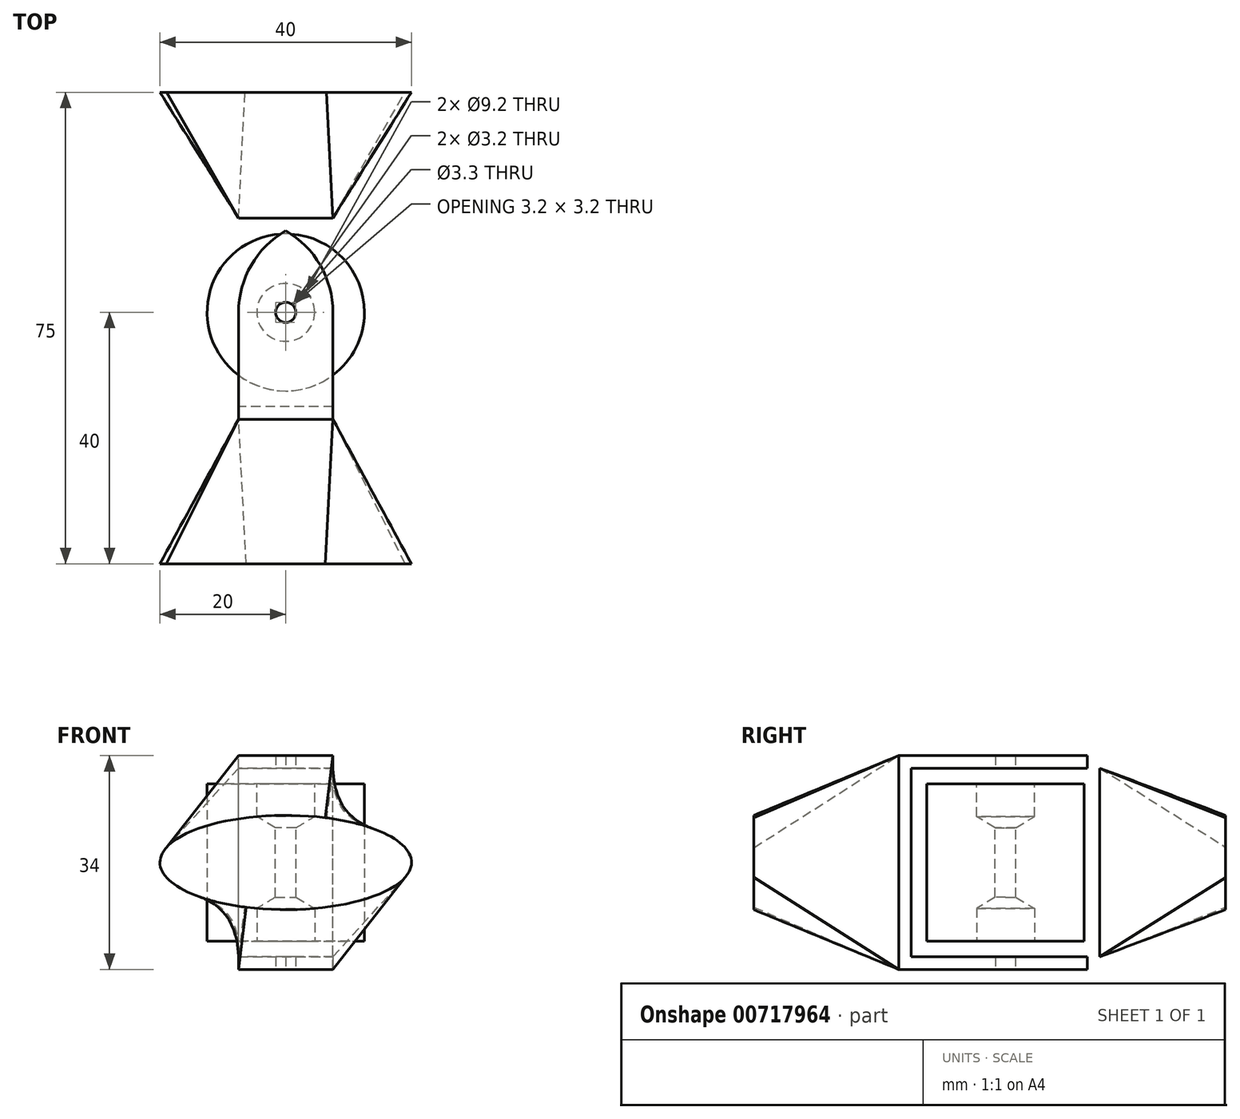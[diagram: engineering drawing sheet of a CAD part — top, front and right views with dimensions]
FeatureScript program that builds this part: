
annotation { "Feature Type Name" : "Feature", "Feature Type Description" : "" }
export const myFeature = defineFeature(function(context is Context, id is Id, definition is map)
    precondition{}
    {
        {
            var Q0;
            Q0=qCreatedBy(makeId("Front.planeOp"),FACE);
            var sketch = newSketch(context, id + "F0", { "sketchPlane" : qUnion([Q0])});
            skLineSegment(sketch, "E0.bottom", {"start": v(7.5, -15) * mm, "end": v(-7.5, -15) * mm});
            skLineSegment(sketch, "E0.top", {"start": v(7.5, 15) * mm, "end": v(-7.5, 15) * mm});
            skLineSegment(sketch, "E0.left", {"start": v(7.5, -15) * mm, "end": v(7.5, 15) * mm});
            skLineSegment(sketch, "E0.right", {"start": v(-7.5, -15) * mm, "end": v(-7.5, 15) * mm});
            skPoint(sketch, "E0.middle", {"position": v(0, 0) * mm});
            skSolve(sketch);
        }
        {
            var Q0;
            Q0 = qSketchRegion(id + "F0", true);
            extrude(context, id + "F1", {"entities" : qUnion([Q0]), "depth" : 2 * mm, "offsetDistance" : 25 * mm});
        }
        {
            var Q0;
            Q0=qCreatedBy(makeId("Top.planeOp"),FACE);
            var sketch = newSketch(context, id + "F2", { "sketchPlane" : qUnion([Q0])});
            skCircle(sketch, "E1", {"center": v(0, 15) * mm, "radius": 12.5 * mm});
            skSolve(sketch);
        }
        {
            var Q0;
            Q0 = qSketchRegion(id + "F2", true);
            extrude(context, id + "F3", {"entities" : qUnion([Q0]), "endBound" : BoundingType.SYMMETRIC, "depth" : 25 * mm, "offsetDistance" : 25 * mm});
        }
        {
            var Q0;
            Q0=makeQuery(id+"F1.opExtrude","CAP_FACE",FACE,{"disambiguationData":[OSD([sQuery(id+"F0.wireOp",EDGE,"E0.bottom"),sQuery(id+"F0.wireOp",EDGE,"E0.top"),sQuery(id+"F0.wireOp",EDGE,"E0.left"),sQuery(id+"F0.wireOp",EDGE,"E0.right")])],"isStart":false});
            var sketch = newSketch(context, id + "F4", { "sketchPlane" : qUnion([Q0])});
            skLineSegment(sketch, "E2.bottom", {"start": v(-7.5, -15) * mm, "end": v(7.5, -15) * mm});
            skLineSegment(sketch, "E2.top", {"start": v(-7.5, -17) * mm, "end": v(7.5, -17) * mm});
            skLineSegment(sketch, "E2.left", {"start": v(7.5, -15) * mm, "end": v(7.5, -17) * mm});
            skLineSegment(sketch, "E2.right", {"start": v(-7.5, -15) * mm, "end": v(-7.5, -17) * mm});
            skLineSegment(sketch, "E3.bottom", {"start": v(-7.5, 15) * mm, "end": v(7.5, 15) * mm});
            skLineSegment(sketch, "E3.top", {"start": v(-7.5, 17) * mm, "end": v(7.5, 17) * mm});
            skLineSegment(sketch, "E3.left", {"start": v(7.5, 15) * mm, "end": v(7.5, 17) * mm});
            skLineSegment(sketch, "E3.right", {"start": v(-7.5, 15) * mm, "end": v(-7.5, 17) * mm});
            skSolve(sketch);
        }
        {
            var Q0;
            Q0 = qSketchRegion(id + "F4", true);
            extrude(context, id + "F5", {"entities" : qUnion([Q0]), "operationType" : NewBodyOperationType.ADD, "oppositeDirection" : true, "depth" : 32 * mm, "offsetDistance" : 25 * mm});
        }
        {
            var Q0;
            Q0=makeQuery(id+"F5.opExtrude","CAP_EDGE",EDGE,{"disambiguationData":[OSD([sQuery(id+"F4.wireOp",EDGE,"E3.right")])],"isStart":false});
            var Q1;
            Q1=makeQuery(id+"F5.opExtrude","CAP_EDGE",EDGE,{"disambiguationData":[OSD([sQuery(id+"F4.wireOp",EDGE,"E3.left")])],"isStart":false});
            var Q2;
            Q2=makeQuery(id+"F5.opExtrude","CAP_EDGE",EDGE,{"disambiguationData":[OSD([sQuery(id+"F4.wireOp",EDGE,"E2.left")])],"isStart":false});
            var Q3;
            Q3=makeQuery(id+"F5.opExtrude","CAP_EDGE",EDGE,{"disambiguationData":[OSD([sQuery(id+"F4.wireOp",EDGE,"E2.right")])],"isStart":false});
            fillet(context, id + "F6", {"entities" : qUnion([Q0, Q1, Q2, Q3]), "radius" : 15 * mm, "tangentPropagation" : true, "allowEdgeOverflow" : false});
        }
        {
            var Q0;
            Q0=makeQuery(id+"F3.opExtrude","CAP_FACE",FACE,{"disambiguationData":[OSD([sQuery(id+"F2.wireOp",EDGE,"E1")])],"isStart":false});
            var sketch = newSketch(context, id + "F7", { "sketchPlane" : qUnion([Q0])});
            skPoint(sketch, "E4", {"position": v(0, 15) * mm});
            skSolve(sketch);
        }
        {
            var Q0;
            Q0=sQuery(id+"F7.wireOp",VERTEX,"E4");
            var Q1;
            Q1=makeQuery(id+"F3.opExtrude","SWEPT_BODY",BODY,{"disambiguationData":[OSD([sQuery(id+"F2.wireOp",EDGE,"E1")])]});
            hole(context, id + "F8", {"style" : HoleStyle.SIMPLE, "endStyle" : HoleEndStyle.THROUGH, "standardTappedOrClearance" : lookupTablePath({ "fit" : "Normal", "standard" : "ISO", "size" : "M3", "type" : "Clearance" }), "standardBlindInLast" : lookupTablePath({ "fit" : "Standard", "standard" : "ISO", "size" : "M3", "type" : "Clearance" }), "holeDiameter" : 3.3 * mm, "majorDiameter" : 5 * mm, "isTappedThrough" : true, "tappedDepth" : 12 * mm, "tapClearance" : 3, "locations" : qUnion([Q0]), "scope" : qUnion([Q1])});
        }
        {
            var Q0;
            Q0=makeQuery(id+"F3.opExtrude","CAP_FACE",FACE,{"disambiguationData":[OSD([sQuery(id+"F2.wireOp",EDGE,"E1")])],"isStart":false});
            var sketch = newSketch(context, id + "F9", { "sketchPlane" : qUnion([Q0])});
            skPoint(sketch, "E5", {"position": v(0, 15) * mm});
            skSolve(sketch);
        }
        {
            var Q0;
            Q0=sQuery(id+"F9.wireOp",VERTEX,"E5");
            var Q1;
            Q1=makeQuery(id+"F3.opExtrude","SWEPT_BODY",BODY,{"disambiguationData":[OSD([sQuery(id+"F2.wireOp",EDGE,"E1")])]});
            hole(context, id + "F10", {"style" : HoleStyle.SIMPLE, "endStyle" : HoleEndStyle.BLIND, "standardTappedOrClearance" : lookupTablePath({ "fit" : "Normal", "standard" : "Custom", "size" : "M5", "type" : "Clearance" }), "standardBlindInLast" : lookupTablePath({ "fit" : "Standard", "standard" : "Custom", "size" : "M5", "type" : "Clearance" }), "holeDiameter" : 9.2 * mm, "majorDiameter" : 5 * mm, "holeDepth" : 5.2 * mm, "isTappedThrough" : true, "tappedDepth" : 12 * mm, "tapClearance" : 3, "locations" : qUnion([Q0]), "scope" : qUnion([Q1])});
        }
        {
            var Q0;
            Q0=makeQuery(id+"F3.opExtrude","CAP_FACE",FACE,{"disambiguationData":[OSD([sQuery(id+"F2.wireOp",EDGE,"E1")])],"isStart":true});
            var sketch = newSketch(context, id + "F11", { "sketchPlane" : qUnion([Q0])});
            skPoint(sketch, "E6", {"position": v(0, -15) * mm});
            skSolve(sketch);
        }
        {
            var Q0;
            Q0=sQuery(id+"F11.wireOp",VERTEX,"E6");
            var Q1;
            Q1=makeQuery(id+"F3.opExtrude","SWEPT_BODY",BODY,{"disambiguationData":[OSD([sQuery(id+"F2.wireOp",EDGE,"E1")])]});
            hole(context, id + "F12", {"style" : HoleStyle.SIMPLE, "endStyle" : HoleEndStyle.BLIND, "holeDiameter" : 9.2 * mm, "majorDiameter" : 5 * mm, "holeDepth" : 5.2 * mm, "isTappedThrough" : true, "tappedDepth" : 12 * mm, "tapClearance" : 3, "locations" : qUnion([Q0]), "scope" : qUnion([Q1])});
        }
        {
            var Q0;
            Q0=makeQuery(id+"F5.opExtrude","SWEPT_FACE",FACE,{"disambiguationData":[OSD([sQuery(id+"F4.wireOp",EDGE,"E2.top")])]});
            var sketch = newSketch(context, id + "F13", { "sketchPlane" : qUnion([Q0])});
            skPoint(sketch, "E7", {"position": v(0, -15) * mm});
            skSolve(sketch);
        }
        {
            var Q0;
            Q0=sQuery(id+"F13.wireOp",VERTEX,"E7");
            var Q1;
            Q1=makeQuery(id+"F1.opExtrude","SWEPT_BODY",BODY,{"disambiguationData":[OSD([sQuery(id+"F0.wireOp",EDGE,"E0.bottom"),sQuery(id+"F0.wireOp",EDGE,"E0.top"),sQuery(id+"F0.wireOp",EDGE,"E0.left"),sQuery(id+"F0.wireOp",EDGE,"E0.right")])]});
            hole(context, id + "F14", {"style" : HoleStyle.SIMPLE, "endStyle" : HoleEndStyle.THROUGH, "holeDiameter" : 3.2 * mm, "majorDiameter" : 5 * mm, "isTappedThrough" : true, "tappedDepth" : 12 * mm, "tapClearance" : 3, "locations" : qUnion([Q0]), "scope" : qUnion([Q1])});
        }
        {
            var Q0;
            Q0=qCreatedBy(makeId("Front.planeOp"),FACE);
            cPlane(context, id + "F15", {"entities" : qUnion([Q0]), "cplaneType" : CPlaneType.OFFSET, "offset" : 25 * mm, "width" : 150 * mm, "height" : 150 * mm});
        }
        {
            var Q0;
            Q0=qCreatedBy(id+"F15.planeOp",FACE);
            var sketch = newSketch(context, id + "F16", { "sketchPlane" : qUnion([Q0])});
            skEllipse(sketch, "E8", {"center": v(0, 0) * mm, "majorRadius": 20 * mm, "minorRadius": 7.5 * mm, "majorAxis": v(1, 0)});
            skSolve(sketch);
        }
        {
            var Q0;
            Q0=makeQuery(id+"F5.boolean.opBoolean","MERGE",FACE,{"derivedFrom":[makeQuery(id+"F1.opExtrude","CAP_FACE",FACE,{"disambiguationData":[OSD([sQuery(id+"F0.wireOp",EDGE,"E0.bottom"),sQuery(id+"F0.wireOp",EDGE,"E0.top"),sQuery(id+"F0.wireOp",EDGE,"E0.left"),sQuery(id+"F0.wireOp",EDGE,"E0.right")])],"isStart":false}),makeQuery(id+"F5.opExtrude","CAP_FACE",FACE,{"disambiguationData":[OSD([sQuery(id+"F4.wireOp",EDGE,"E2.bottom"),sQuery(id+"F4.wireOp",EDGE,"E2.top"),sQuery(id+"F4.wireOp",EDGE,"E2.left"),sQuery(id+"F4.wireOp",EDGE,"E2.right")])],"isStart":true}),makeQuery(id+"F5.opExtrude","CAP_FACE",FACE,{"disambiguationData":[OSD([sQuery(id+"F4.wireOp",EDGE,"E3.bottom"),sQuery(id+"F4.wireOp",EDGE,"E3.top"),sQuery(id+"F4.wireOp",EDGE,"E3.left"),sQuery(id+"F4.wireOp",EDGE,"E3.right")])],"isStart":true})]});
            var sketch = newSketch(context, id + "F17", { "sketchPlane" : qUnion([Q0])});
            skLineSegment(sketch, "E9.bottom", {"start": v(-7.5, 17) * mm, "end": v(7.5, 17) * mm});
            skLineSegment(sketch, "E9.top", {"start": v(-7.5, -17) * mm, "end": v(7.5, -17) * mm});
            skLineSegment(sketch, "E9.left", {"start": v(-7.5, 17) * mm, "end": v(-7.5, -17) * mm});
            skLineSegment(sketch, "E9.right", {"start": v(7.5, 17) * mm, "end": v(7.5, -17) * mm});
            skSolve(sketch);
        }
        {
            var Q1;
            Q1 = qSketchRegion(id + "F16", true);
            var Q2;
            Q2 = qSketchRegion(id + "F17", true);
            loft(context, id + "F18", {"operationType" : NewBodyOperationType.ADD, "sheetProfilesArray" : [{ "sheetProfileEntities" : qUnion([Q1]) }, { "sheetProfileEntities" : qUnion([Q2]) }]});
        }
        {
            var Q0;
            Q0=qCreatedBy(id+"F15.planeOp",FACE);
            cPlane(context, id + "F19", {"entities" : qUnion([Q0]), "cplaneType" : CPlaneType.OFFSET, "offset" : 75 * mm, "oppositeDirection" : true, "width" : 150 * mm, "height" : 150 * mm});
        }
        {
            var Q0;
            Q0=qCreatedBy(id+"F19.planeOp",FACE);
            var sketch = newSketch(context, id + "F20", { "sketchPlane" : qUnion([Q0])});
            skEllipse(sketch, "E10", {"center": v(0, 0) * mm, "majorRadius": 20 * mm, "minorRadius": 7.5 * mm, "majorAxis": v(-1, 0)});
            skSolve(sketch);
        }
        {
            var Q0;
            Q0=qCreatedBy(makeId("Front.planeOp"),FACE);
            cPlane(context, id + "F21", {"entities" : qUnion([Q0]), "cplaneType" : CPlaneType.OFFSET, "offset" : 30 * mm, "oppositeDirection" : true, "width" : 150 * mm, "height" : 150 * mm});
        }
        {
            var Q0;
            Q0=qCreatedBy(id+"F21.planeOp",FACE);
            var sketch = newSketch(context, id + "F22", { "sketchPlane" : qUnion([Q0])});
            skLineSegment(sketch, "E11.bottom", {"start": v(-7.5, -15) * mm, "end": v(7.5, -15) * mm});
            skLineSegment(sketch, "E11.top", {"start": v(-7.5, 15) * mm, "end": v(7.5, 15) * mm});
            skLineSegment(sketch, "E11.left", {"start": v(-7.5, -15) * mm, "end": v(-7.5, 15) * mm});
            skLineSegment(sketch, "E11.right", {"start": v(7.5, -15) * mm, "end": v(7.5, 15) * mm});
            skPoint(sketch, "E11.middle", {"position": v(0, 0) * mm});
            skSolve(sketch);
        }
        {
            var Q0;
            Q0 = qSketchRegion(id + "F22", true);
            var Q1;
            Q1 = qSketchRegion(id + "F20", true);
            loft(context, id + "F23", {"sheetProfilesArray" : [{ "sheetProfileEntities" : qUnion([Q0]) }, { "sheetProfileEntities" : qUnion([Q1]) }]});
        }
    });
